# Revit family: Shower-Shower_Arm-KOHLER-K-26318
name_source: partatom
category: Plumbing Fixtures
revit_build: Autodesk Revit 2017 (Build: 20160225_1515(x64)
units: mm (PartAtom-declared; Revit-internal decimal feet)

## family parameters
Cut with Voids When Loaded = No
Host = Face
OmniClass Number = 23.31.25.00
OmniClass Title = Toilet and Bath Specialties
Part Type = Normal
Room Calculation Point = No
Round Connector Dimension = Use Diameter
Shared = No

## types (4) — shared parameters
ADA Compliant = No
Assembly Code = D2010700
CW Connection = Yes
Cold Water Inlet = Cold Water Inlet
Date Modified = 02/08/2020
Description = Shower Arm
Drain Included = No
Flow Rate = 0 GPM
HW Connection = Yes
Height = 3"
Hot Water Inlet = Hot Water Inlet
Length = 5 13/16"
Manufacturer = KOHLER Co.
Master Format 2014 = 22 42 23
Master Format 2014 Name = Residential Showers
Material = Brass Construction
Pressure = 0.00 psi
Product Documentation Link = https://www.us.kohler.com
Product Page URL = http://www.us.kohler.com
URL = https://www.us.kohler.com
Vent Connection = No
Waste Connection = No
Waste Water Outlet = Waste Water Outlet
WaterSense Certified = No
Width = 2 3/16"

## per-type parameters (varying)
| type | Default Elevation | Finish | Model | Type |
| CP-Polished Chrome | 72" | Kohler-Metal-CP-Polished_Chrome | K-26318-CP | 1 |
| BL-Matte Black | 0" | Kohler-Metal-BL-Matte_Black | K-26318-BL | 2 |
| BN-Vibrant Brushed Nickel | 0" | Kohler-Metal-BN-Vibrant_Brushed_Nickel | K-26318-BN | 3 |
| 2MB-Vibrant Brushed Moderne Brass | 0" | Kohler-Metal-2MB-Vibrant_Brushed_Moderne_Brass | K-26318-2MB | 4 |

## geometry (parser evidence)
native form markers: Sweep x6
no freeform markers — native parametric forms only
